# Revit family: Шаровой кран с рычажной рукояткой и обратным клапаном 2110
name_source: partatom
category: Rohrzubehör
units: mm (PartAtom-declared; Revit-internal decimal feet)

## family parameters
Arbeitsebenenbasiert = Nein
Beim Laden mit Abzugskörper schneiden = Nein
Bemaßung runder Anschluss = Durchmesser verwenden
Gemeinsam genutzt = Nein
Immer vertikal = Ja
OmniClass-Nummer = 23.65.55.14
OmniClass-Titel = Valves for Liquid Services
Teiletyp = Unterbricht

## types (1)
- Шаровой кран с рычажной рукояткой и обратным клапаном 2110
    Hersteller = HERZ Armaturen Ges.m.b.H.
    L03 = 5 mm  [stored 0.0164042 ft]
    O-Ring обратного клапана = силикон
    R01 = 7 mm  [stored 0.0229659 ft]
    S04 = 5 mm  [stored 0.0164042 ft]
    SCTWCODE = 04;04;02
    SCTWSEQ = FW;SBT_TYP_FW="102";2
    SC_NennweiteBerechnet = 0
    URL = www.herz-armaturen.ru
    W01 = 45.00°
    Корпус = штампованная латунь, устойчивая к селективной цинковой коррозии, согласно EN 12165, CW626N
    Корпус обратного клапана = POM
    Макс. рабочая температура = 85 °C
    Макс. рабочее давление = 2500000.0 Pa
    Мин. рабочая температура = -10 °C
    Мин. рабочая температура (вода) = 1 °C
    Область применения = Шаровой кран с рычажной рукояткой и обратным клапаном применяется в системах питьевого водоснабжения и служит запорным устройством.
Как правило, шаровые краны используются в системах для надежного перекрытия трубопровода.
Обратный клапан гарантирует движение потока только в одном направлении, указанном стрелкой на корпусе крана.
    Примечание = В соответствии со статьей 33 Регламента REACH (Registration; Evaluation; Authorisation; Restriction of Chemicals) (EC № 1907/2006) мы обязаны указать, что свинец внесен в список SVHC (Substances of Very High Concern - вещества очень высокой важности) и весовой процент свинца во всех латунных компонентах заводского изготовления в наших изделиях, превышает 0,1 % (w/w) (CAS: 7439-92-1 / EINECS: 231-100-4).
Поскольку свинец является легирующим компонентом сплава, прямое негативное влияние исключается, и поэтому дополнительной информации о безопасном использовании не требуется.
    Резьба = согласно  ISO 228
    Рукоятка = рычажная рукоятка, цвет - зеленый, оцинкованная сталь
    Среда = Питьевая вода
    Уплотнение шара = PTFE
    Уплотнение шпинделя = EPDM
    Шар = штампованная латунь, устойчивая к селективной цинковой коррозии, согласно EN 12165, хромированный полнопроходной шар, CW626N
    Шпиндель = латунь в соответствии с EN 12164, CW614N

note: [stored X ft] marks values corroborated as IEEE doubles in the binary element streams (Revit-internal decimal feet)
